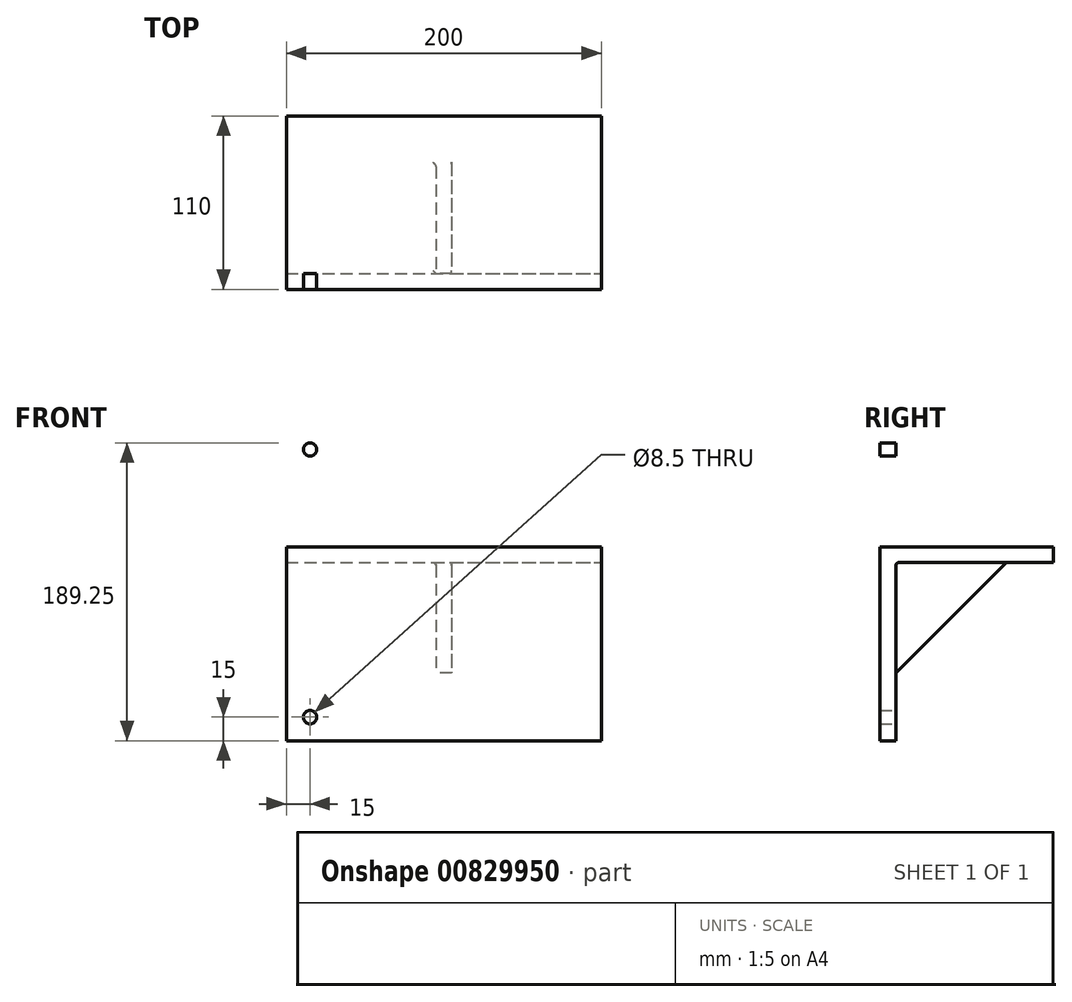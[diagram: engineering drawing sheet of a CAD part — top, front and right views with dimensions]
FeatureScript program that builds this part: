
annotation { "Feature Type Name" : "Feature", "Feature Type Description" : "" }
export const myFeature = defineFeature(function(context is Context, id is Id, definition is map)
    precondition{}
    {
        {
            var Q0;
            Q0=qCreatedBy(makeId("Front.planeOp"),FACE);
            var sketch = newSketch(context, id + "F0", { "sketchPlane" : qUnion([Q0])});
            skLineSegment(sketch, "E0.bottom", {"start": v(-100, 100) * mm, "end": v(100, 100) * mm});
            skLineSegment(sketch, "E0.top", {"start": v(-100, -100) * mm, "end": v(100, -100) * mm});
            skLineSegment(sketch, "E0.left", {"start": v(-100, 100) * mm, "end": v(-100, -100) * mm});
            skLineSegment(sketch, "E0.right", {"start": v(100, 100) * mm, "end": v(100, -100) * mm});
            skPoint(sketch, "E0.middle", {"position": v(0, 0) * mm});
            skSolve(sketch);
        }
        {
            var Q0;
            Q0 = qSketchRegion(id + "F0", true);
            extrude(context, id + "F1", {"entities" : qUnion([Q0]), "depth" : 110 * mm, "offsetDistance" : 25 * mm});
        }
        {
            var Q0;
            Q0=makeQuery(id+"F1.opExtrude","SWEPT_FACE",FACE,{"disambiguationData":[OSD([sQuery(id+"F0.wireOp",EDGE,"E0.right")])]});
            var sketch = newSketch(context, id + "F2", { "sketchPlane" : qUnion([Q0])});
            skLineSegment(sketch, "E1", {"start": v(-100, 100) * mm, "end": v(-100, -100) * mm});
            skLineSegment(sketch, "E2", {"start": v(-100, 23.2) * mm, "end": v(0, 23.2) * mm});
            skLineSegment(sketch, "E3", {"start": v(-100, 13.2) * mm, "end": v(0, 13.2) * mm});
            skSolve(sketch);
        }
        {
            var Q0;
            Q0 = qSketchRegion(id + "F2", true);
            var Q1;
            {var subQ4=sQuery(id+"F2.wireOp",EDGE,"E2");Q1=makeQuery(id+"F2.imprint","IMPRINT",FACE,{"disambiguationData":[TD([[makeQuery(id+"F2.imprint","IMPRINT",EDGE,{"derivedFrom":subQ4}),1.0]])]});}
            var Q2;
            {var subQ4=sQuery(id+"F2.wireOp",EDGE,"E3");Q2=makeQuery(id+"F2.imprint","IMPRINT",FACE,{"disambiguationData":[TD([[makeQuery(id+"F2.imprint","IMPRINT",EDGE,{"derivedFrom":subQ4}),-1.0]])]});}
            extrude(context, id + "F3", {"entities" : qUnion([Q0, Q1, Q2]), "operationType" : NewBodyOperationType.REMOVE, "oppositeDirection" : true, "depth" : 200 * mm, "offsetDistance" : 25 * mm});
        }
        {
            var Q0;
            {var subQ0=sQuery(id+"F2.wireOp",EDGE,"E1");Q0=makeQuery(id+"F3.boolean.opBoolean","COPY",FACE,{"derivedFrom":makeQuery(id+"F3.opExtrude","SWEPT_FACE",FACE,{"disambiguationData":[OSD([subQ0]),TDD([makeQuery(id+"F2.imprint","IMPRINT",EDGE,{"disambiguationData":[TD([[makeQuery(id+"F2.imprint","INTERSECT",VERTEX,{"derivedFrom":[subQ0,sQuery(id+"F2.wireOp",EDGE,"E3")]}),-1.0]])],"derivedFrom":subQ0})])]})});}
            var sketch = newSketch(context, id + "F4", { "sketchPlane" : qUnion([Q0])});
            skLineSegment(sketch, "E4", {"start": v(-5, 13.2) * mm, "end": v(-5, -56.8) * mm});
            skLineSegment(sketch, "E5.MirrorCS", {"start": v(5, 13.2) * mm, "end": v(5, -56.8) * mm});
            skLineSegment(sketch, "E6", {"start": v(-5, -56.8) * mm, "end": v(5, -56.8) * mm});
            skSolve(sketch);
        }
        {
            var Q0;
            Q0 = qSketchRegion(id + "F4", true);
            var Q1;
            {var subQ0=sQuery(id+"F4.wireOp",EDGE,"E4");Q1=makeQuery(id+"F4.imprint","IMPRINT",FACE,{"disambiguationData":[TD([[makeQuery(id+"F4.imprint","IMPRINT",EDGE,{"derivedFrom":subQ0}),1.0]])]});}
            extrude(context, id + "F5", {"entities" : qUnion([Q0, Q1]), "operationType" : NewBodyOperationType.ADD, "depth" : 100 * mm, "offsetDistance" : 25 * mm});
        }
        {
            var Q0;
            Q0=makeQuery(id+"F5.opExtrude","SWEPT_FACE",FACE,{"disambiguationData":[OSD([sQuery(id+"F4.wireOp",EDGE,"E4")])]});
            var sketch = newSketch(context, id + "F6", { "sketchPlane" : qUnion([Q0])});
            skLineSegment(sketch, "E7", {"start": v(-30, 13.2) * mm, "end": v(-100, -56.8) * mm});
            skLineSegment(sketch, "E8", {"start": v(-30, 13.2) * mm, "end": v(0, 13.2) * mm});
            skLineSegment(sketch, "E9", {"start": v(0, 13.2) * mm, "end": v(0, -56.8) * mm});
            skLineSegment(sketch, "E10", {"start": v(0, -56.8) * mm, "end": v(-100, -56.8) * mm});
            skSolve(sketch);
        }
        {
            var Q0;
            Q0=makeQuery(id+"F6.imprint","IMPRINT",FACE,{"disambiguationData":[TD([[makeQuery(id+"F6.imprint","IMPRINT",EDGE,{"derivedFrom":sQuery(id+"F6.wireOp",EDGE,"E7")}),1.0]])]});
            extrude(context, id + "F7", {"entities" : qUnion([Q0]), "operationType" : NewBodyOperationType.REMOVE, "oppositeDirection" : true, "depth" : 200 * mm, "offsetDistance" : 25 * mm});
        }
        {
            var Q0;
            {var subQ0=sQuery(id+"F2.wireOp",EDGE,"E1");Q0=makeQuery(id+"F3.boolean.opBoolean","COPY",FACE,{"derivedFrom":makeQuery(id+"F3.opExtrude","SWEPT_FACE",FACE,{"disambiguationData":[OSD([subQ0]),TDD([makeQuery(id+"F2.imprint","IMPRINT",EDGE,{"disambiguationData":[TD([[makeQuery(id+"F2.imprint","INTERSECT",VERTEX,{"derivedFrom":[subQ0,sQuery(id+"F2.wireOp",EDGE,"E2")]}),1.0]])],"derivedFrom":subQ0})])]})});}
            var sketch = newSketch(context, id + "F8", { "sketchPlane" : qUnion([Q0])});
            skCircle(sketch, "E11", {"center": v(-85, 85) * mm, "radius": 4.25 * mm});
            skCircle(sketch, "E12.MirrorC", {"center": v(85, 85) * mm, "radius": 4.25 * mm});
            skCircle(sketch, "E13.MirrorC", {"center": v(-85, -85) * mm, "radius": 4.25 * mm});
            skCircle(sketch, "E14.MirrorC", {"center": v(85, -85) * mm, "radius": 4.25 * mm});
            skSolve(sketch);
        }
        {
            var Q0;
            Q0=makeQuery(id+"F8.imprint","IMPRINT",FACE,{"disambiguationData":[TD([[makeQuery(id+"F8.imprint","IMPRINT",EDGE,{"derivedFrom":sQuery(id+"F8.wireOp",EDGE,"E11")}),1.0]])]});
            var Q1;
            Q1=makeQuery(id+"F8.imprint","IMPRINT",FACE,{"disambiguationData":[TD([[makeQuery(id+"F8.imprint","IMPRINT",EDGE,{"derivedFrom":sQuery(id+"F8.wireOp",EDGE,"E12.MirrorC")}),-1.0]])]});
            var Q2;
            Q2=makeQuery(id+"F8.imprint","IMPRINT",FACE,{"disambiguationData":[TD([[makeQuery(id+"F8.imprint","IMPRINT",EDGE,{"derivedFrom":sQuery(id+"F8.wireOp",EDGE,"E14.MirrorC")}),1.0]])]});
            var Q3;
            Q3=makeQuery(id+"F8.imprint","IMPRINT",FACE,{"disambiguationData":[TD([[makeQuery(id+"F8.imprint","IMPRINT",EDGE,{"derivedFrom":sQuery(id+"F8.wireOp",EDGE,"E13.MirrorC")}),-1.0]])]});
            extrude(context, id + "F9", {"entities" : qUnion([Q0, Q1, Q2, Q3]), "operationType" : NewBodyOperationType.REMOVE, "oppositeDirection" : true, "depth" : 10 * mm, "offsetDistance" : 25 * mm});
        }
        {
            var Q0;
            Q0=makeQuery(id+"F3.boolean.opBoolean","COPY",EDGE,{"derivedFrom":makeQuery(id+"F3.opExtrude","SWEPT_EDGE",EDGE,{"disambiguationData":[OSD([sQuery(id+"F2.wireOp",EDGE,"E1"),sQuery(id+"F2.wireOp",EDGE,"E2")])]})});
            var Q1;
            {var subQ0=sQuery(id+"F0.wireOp",EDGE,"E0.right");var subQ1=sQuery(id+"F2.wireOp",EDGE,"E1");var subQ2=sQuery(id+"F2.wireOp",EDGE,"E3");Q1=makeQuery(id+"F5.boolean.opBoolean","SPLIT",EDGE,{"disambiguationData":[TD([makeQuery(id+"F1.opExtrude","SWEPT_FACE",FACE,{"disambiguationData":[OSD([subQ0])]})])],"derivedFrom":makeQuery(id+"F3.boolean.opBoolean","COPY",EDGE,{"derivedFrom":makeQuery(id+"F3.opExtrude","SWEPT_EDGE",EDGE,{"disambiguationData":[OSD([subQ1,subQ2])]})})});}
            var Q2;
            Q2=makeQuery(id+"F5.opExtrude","CAP_EDGE",EDGE,{"disambiguationData":[OSD([sQuery(id+"F4.wireOp",EDGE,"E4")])],"isStart":true});
            var Q3;
            Q3=makeQuery(id+"F5.opExtrude","SWEPT_EDGE",EDGE,{"disambiguationData":[OSD([sQuery(id+"F2.wireOp",EDGE,"E1"),sQuery(id+"F2.wireOp",EDGE,"E3"),sQuery(id+"F4.wireOp",EDGE,"E4")])]});
            var Q4;
            Q4=makeQuery(id+"F7.boolean.opBoolean","COPY",EDGE,{"derivedFrom":makeQuery(id+"F7.opExtrude","SWEPT_EDGE",EDGE,{"disambiguationData":[OSD([sQuery(id+"F2.wireOp",EDGE,"E1"),sQuery(id+"F2.wireOp",EDGE,"E3"),sQuery(id+"F4.wireOp",EDGE,"E4"),sQuery(id+"F6.wireOp",EDGE,"E7"),sQuery(id+"F6.wireOp",EDGE,"E8")])]})});
            var Q5;
            Q5=makeQuery(id+"F7.boolean.opBoolean","MERGE",EDGE,{"derivedFrom":[makeQuery(id+"F5.opExtrude","CAP_EDGE",EDGE,{"disambiguationData":[OSD([sQuery(id+"F4.wireOp",EDGE,"E6")])],"isStart":true}),makeQuery(id+"F7.opExtrude","SWEPT_EDGE",EDGE,{"disambiguationData":[OSD([sQuery(id+"F4.wireOp",EDGE,"E4"),sQuery(id+"F6.wireOp",EDGE,"E7"),sQuery(id+"F6.wireOp",EDGE,"E10")])]})]});
            var Q6;
            Q6=makeQuery(id+"F5.opExtrude","SWEPT_EDGE",EDGE,{"disambiguationData":[OSD([sQuery(id+"F2.wireOp",EDGE,"E1"),sQuery(id+"F2.wireOp",EDGE,"E3"),sQuery(id+"F4.wireOp",EDGE,"E5.MirrorCS")])]});
            var Q7;
            Q7=makeQuery(id+"F5.opExtrude","CAP_EDGE",EDGE,{"disambiguationData":[OSD([sQuery(id+"F4.wireOp",EDGE,"E5.MirrorCS")])],"isStart":true});
            var Q8;
            {var subQ0=sQuery(id+"F2.wireOp",EDGE,"E1");var subQ1=sQuery(id+"F2.wireOp",EDGE,"E3");Q8=makeQuery(id+"F5.boolean.opBoolean","SPLIT",EDGE,{"disambiguationData":[TD([makeQuery(id+"F1.opExtrude","SWEPT_FACE",FACE,{"disambiguationData":[OSD([sQuery(id+"F0.wireOp",EDGE,"E0.left")])]})])],"derivedFrom":makeQuery(id+"F3.boolean.opBoolean","COPY",EDGE,{"derivedFrom":makeQuery(id+"F3.opExtrude","SWEPT_EDGE",EDGE,{"disambiguationData":[OSD([subQ0,subQ1])]})})});}
            fillet(context, id + "F10", {"entities" : qUnion([Q0, Q1, Q2, Q3, Q4, Q5, Q6, Q7, Q8]), "radius" : 2 * mm, "tangentPropagation" : true, "allowEdgeOverflow" : false});
        }
    });
